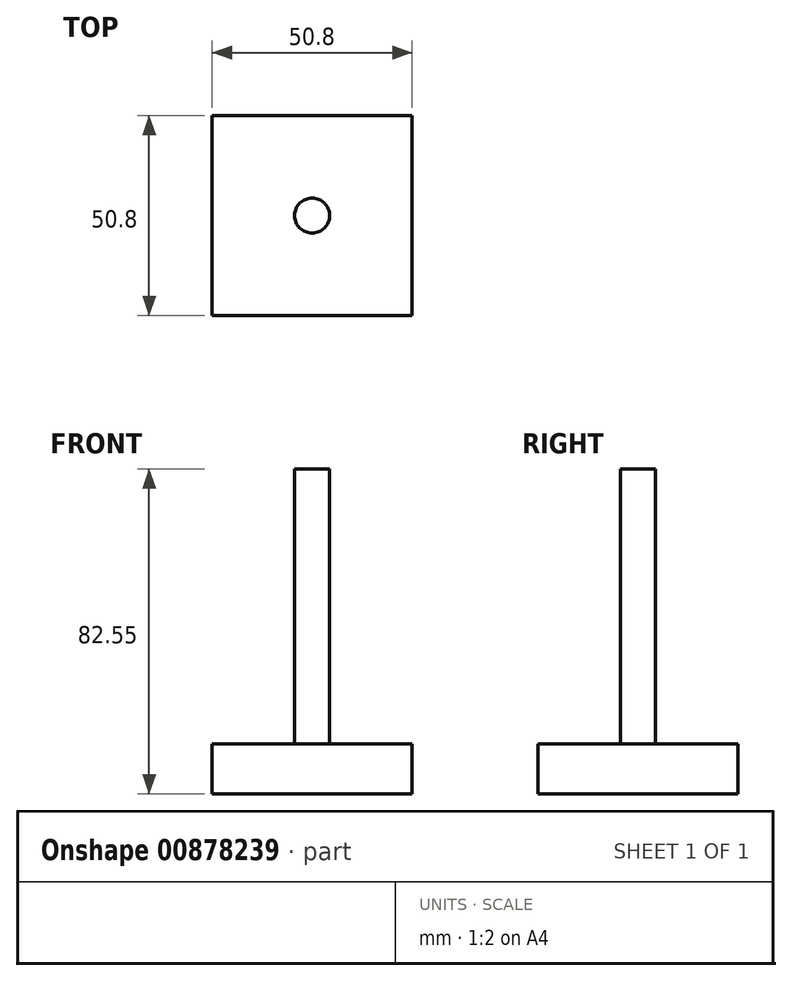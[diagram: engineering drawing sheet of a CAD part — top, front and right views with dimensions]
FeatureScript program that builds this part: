
annotation { "Feature Type Name" : "Feature", "Feature Type Description" : "" }
export const myFeature = defineFeature(function(context is Context, id is Id, definition is map)
    precondition{}
    {
        {
            var Q0;
            Q0=qCreatedBy(makeId("Front.planeOp"),FACE);
            var sketch = newSketch(context, id + "F0", { "sketchPlane" : qUnion([Q0])});
            skLineSegment(sketch, "E0.bottom", {"start": v(-25.4, 6.35) * mm, "end": v(25.4, 6.35) * mm});
            skLineSegment(sketch, "E0.top", {"start": v(-25.4, -6.35) * mm, "end": v(25.4, -6.35) * mm});
            skLineSegment(sketch, "E0.left", {"start": v(-25.4, 6.35) * mm, "end": v(-25.4, -6.35) * mm});
            skLineSegment(sketch, "E0.right", {"start": v(25.4, 6.35) * mm, "end": v(25.4, -6.35) * mm});
            skPoint(sketch, "E0.middle", {"position": v(0, 0) * mm});
            skSolve(sketch);
        }
        {
            var Q0;
            Q0=makeQuery(id+"F0.imprint","IMPRINT",FACE,{"disambiguationData":[TD([[makeQuery(id+"F0.imprint","IMPRINT",EDGE,{"derivedFrom":sQuery(id+"F0.wireOp",EDGE,"E0.bottom")}),-1.0]])]});
            extrude(context, id + "F1", {"entities" : qUnion([Q0]), "endBound" : BoundingType.SYMMETRIC, "depth" : 50.8 * mm, "offsetDistance" : 25.4 * mm});
        }
        {
            var Q0;
            Q0=qCreatedBy(makeId("Top.planeOp"),FACE);
            var sketch = newSketch(context, id + "F2", { "sketchPlane" : qUnion([Q0])});
            skCircle(sketch, "E1", {"center": v(0, 0) * mm, "radius": 4.45 * mm});
            skSolve(sketch);
        }
        {
            var Q0;
            Q0 = qSketchRegion(id + "F2", true);
            extrude(context, id + "F3", {"entities" : qUnion([Q0]), "operationType" : NewBodyOperationType.ADD, "depth" : 76.2 * mm, "offsetDistance" : 25.4 * mm});
        }
    });
